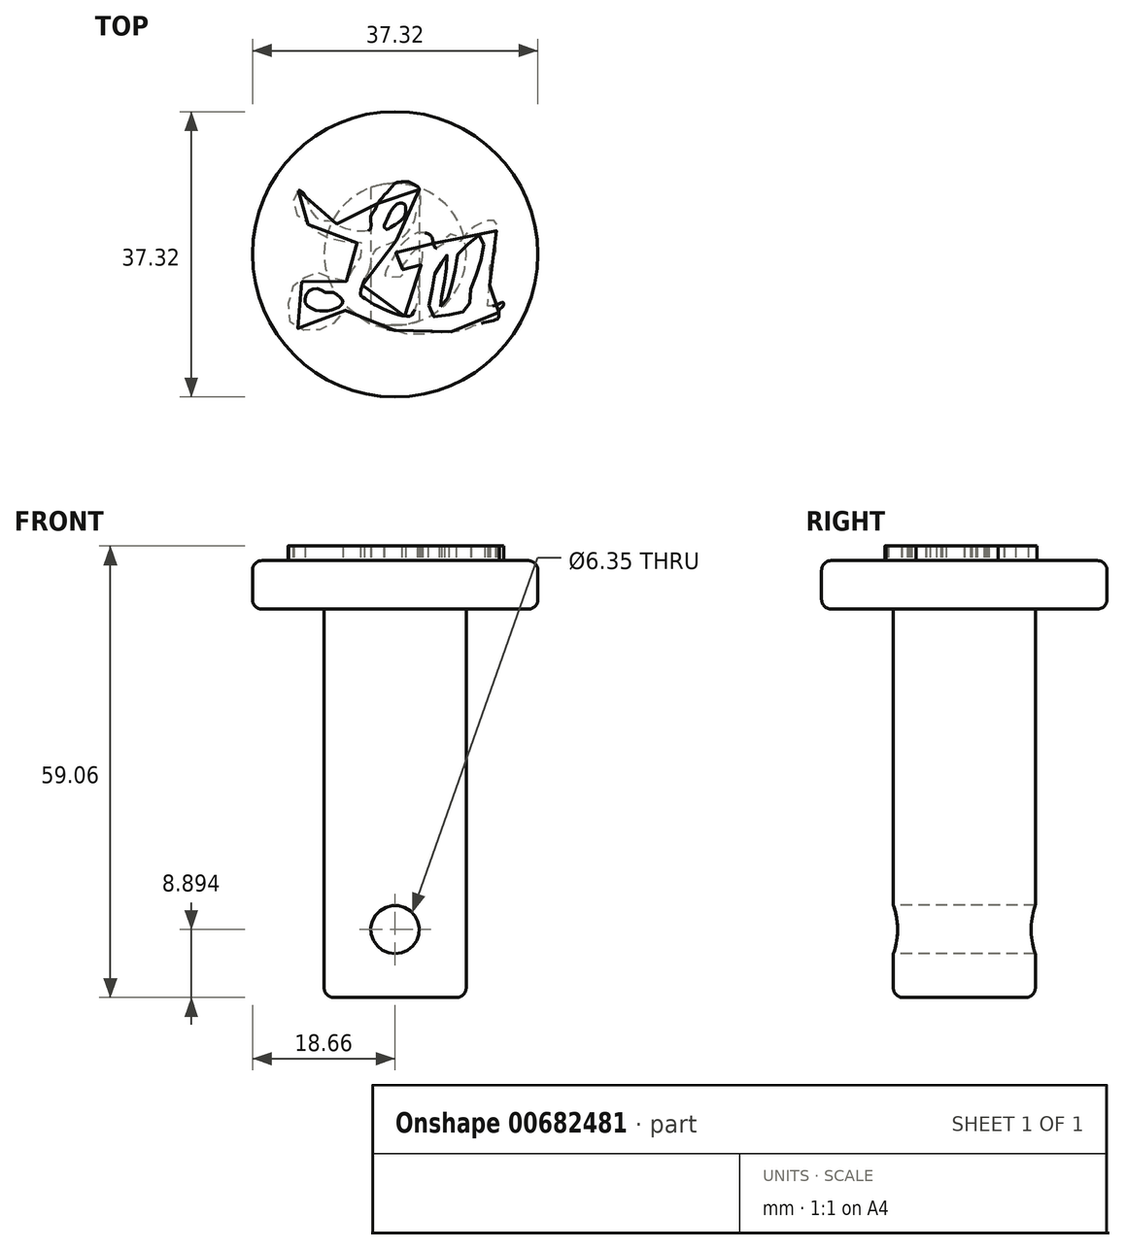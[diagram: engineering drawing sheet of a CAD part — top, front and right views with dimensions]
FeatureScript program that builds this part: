
annotation { "Feature Type Name" : "Feature", "Feature Type Description" : "" }
export const myFeature = defineFeature(function(context is Context, id is Id, definition is map)
    precondition{}
    {
        {
            var Q0;
            Q0=qCreatedBy(makeId("Top.planeOp"),FACE);
            var sketch = newSketch(context, id + "F0", { "sketchPlane" : qUnion([Q0])});
            skCircle(sketch, "E0", {"center": v(0, 0) * mm, "radius": 18.66 * mm});
            skSolve(sketch);
        }
        {
            var Q0;
            Q0=makeQuery(id+"F0.imprint","IMPRINT",FACE,{"disambiguationData":[TD([[makeQuery(id+"F0.imprint","IMPRINT",EDGE,{"derivedFrom":sQuery(id+"F0.wireOp",EDGE,"E0")}),1.0]])]});
            extrude(context, id + "F1", {"entities" : qUnion([Q0]), "depth" : 6.35 * mm, "offsetDistance" : 25.4 * mm});
        }
        {
            var Q0;
            Q0=makeQuery(id+"F1.opExtrude","CAP_FACE",FACE,{"disambiguationData":[OSD([sQuery(id+"F0.wireOp",EDGE,"E0")])],"isStart":true});
            var sketch = newSketch(context, id + "F2", { "sketchPlane" : qUnion([Q0])});
            skCircle(sketch, "E1", {"center": v(0, 0) * mm, "radius": 9.28 * mm});
            skSolve(sketch);
        }
        {
            var Q0;
            Q0=makeQuery(id+"F2.imprint","IMPRINT",FACE,{"disambiguationData":[TD([[makeQuery(id+"F2.imprint","IMPRINT",EDGE,{"derivedFrom":sQuery(id+"F2.wireOp",EDGE,"E1")}),1.0]])]});
            extrude(context, id + "F3", {"entities" : qUnion([Q0]), "operationType" : NewBodyOperationType.ADD, "depth" : 50.8 * mm, "offsetDistance" : 25.4 * mm});
        }
        {
            var Q0;
            Q0=qCreatedBy(makeId("Front.planeOp"),FACE);
            cPlane(context, id + "F4", {"entities" : qUnion([Q0]), "cplaneType" : CPlaneType.OFFSET, "offset" : 19.05 * mm, "width" : 152.4 * mm, "height" : 152.4 * mm});
        }
        {
            var Q0;
            Q0=qCreatedBy(id+"F4.planeOp",FACE);
            var sketch = newSketch(context, id + "F5", { "sketchPlane" : qUnion([Q0])});
            skCircle(sketch, "E2", {"center": v(0, -41.9) * mm, "radius": 3.72 * mm});
            skSolve(sketch);
        }
        {
            var Q0;
            Q0=sQuery(id+"F5.wireOp",VERTEX,"E2.center");
            var Q1;
            Q1=makeQuery(id+"F1.opExtrude","SWEPT_BODY",BODY,{"disambiguationData":[OSD([sQuery(id+"F0.wireOp",EDGE,"E0")])]});
            hole(context, id + "F6", {"style" : HoleStyle.SIMPLE, "endStyle" : HoleEndStyle.THROUGH, "holeDiameter" : 6.35 * mm, "majorDiameter" : 6.35 * mm, "isTappedThrough" : true, "tappedDepth" : 12.7 * mm, "tapClearance" : 3, "locations" : qUnion([Q0]), "scope" : qUnion([Q1])});
        }
        {
            var Q0;
            Q0=makeQuery(id+"F1.opExtrude","CAP_FACE",FACE,{"disambiguationData":[OSD([sQuery(id+"F0.wireOp",EDGE,"E0")])],"isStart":false});
            var sketch = newSketch(context, id + "F7", { "sketchPlane" : qUnion([Q0])});
            skFitSpline(sketch, "E3", {"points": [v(-12.67, 8.37) * mm, v(-13.23, 8.26) * mm, v(-13.23, 7.76) * mm, v(-13.28, 6.99) * mm, v(-13.34, 6.33) * mm, v(-13.11, 5.61) * mm, v(-12.73, 5.17) * mm, v(-12.4, 5.28) * mm, v(-12.12, 4.95) * mm, v(-11.74, 4.4) * mm, v(-11.46, 3.96) * mm, v(-10.96, 3.62) * mm, v(-10.52, 3.13) * mm, v(-9.86, 2.63) * mm, v(-9.36, 2.36) * mm, v(-8.54, 2.08) * mm, v(-7.6, 1.75) * mm, v(-6.6, 1.64) * mm, v(-5.5, 1.47) * mm, v(-4.84, 1.53) * mm, v(-4.34, 1.53) * mm, v(-4.01, 1.2) * mm, v(-4.34, 0) * mm, v(-4.78, -0.79) * mm, v(-5, -1.18) * mm, v(-5.34, -1.62) * mm, v(-5.61, -2.22) * mm, v(-5.89, -2.89) * mm, v(-6.27, -3.44) * mm, v(-6.6, -3.66) * mm, v(-7.38, -3.44) * mm, v(-8.2, -3.16) * mm, v(-9.09, -2.78) * mm, v(-9.75, -2.5) * mm, v(-10.36, -2.39) * mm, v(-11.02, -2.5) * mm, v(-11.74, -2.89) * mm, v(-12.07, -3.5) * mm, v(-12.62, -3.82) * mm, v(-13.28, -4.15) * mm, v(-13.72, -4.76) * mm, v(-14, -5.97) * mm, v(-13.94, -7.24) * mm, v(-13.94, -8.13) * mm, v(-13.72, -8.95) * mm, v(-13.06, -9.56) * mm, v(-12.07, -9.84) * mm, v(-11.07, -9.95) * mm, v(-10.3, -9.9) * mm, v(-9.36, -9.73) * mm, v(-8.65, -9.62) * mm, v(-7.98, -9) * mm, v(-7.27, -8.51) * mm, v(-6.77, -7.74) * mm, v(-6.27, -7.19) * mm, v(-5.78, -7.46) * mm, v(-5.23, -7.85) * mm, v(-4.45, -8.13) * mm, v(-3.8, -8.84) * mm, v(-2.85, -9.23) * mm, v(-2.03, -9.28) * mm, v(-1.42, -9.62) * mm, v(0, -9.95) * mm, v(1.28, -10.33) * mm, v(2.17, -10.39) * mm, v(2.94, -10.39) * mm, v(4.04, -10.39) * mm, v(4.7, -10.28) * mm, v(5.7, -10.17) * mm, v(6.41, -10.22) * mm, v(7.3, -10.11) * mm, v(7.96, -10) * mm, v(9, -9.9) * mm, v(10, -9.45) * mm, v(10.94, -9.12) * mm, v(12.04, -8.84) * mm, v(12.98, -8.62) * mm, v(13.53, -8.3) * mm, v(13.59, -7.8) * mm, v(13.64, -7.24) * mm, v(14.14, -6.75) * mm, v(14.08, -6.3) * mm, v(13.47, -6.53) * mm, v(12.87, -6.75) * mm, v(12.15, -6.91) * mm, v(12.1, -6.75) * mm, v(12.2, -5.86) * mm, v(12.2, -5.1) * mm, v(12.37, -4.1) * mm, v(12.37, -3.38) * mm, v(12.43, -2.44) * mm, v(12.26, -2) * mm, v(12.54, -1.34) * mm, v(12.81, -0.46) * mm, v(13.25, 0.7) * mm, v(13.14, 1.53) * mm, v(13.2, 2.74) * mm, v(13.3, 3.9) * mm, v(13.25, 4.34) * mm, v(12.76, 4.4) * mm, v(12.26, 4.4) * mm, v(11.49, 4.18) * mm, v(10.88, 3.84) * mm, v(10.33, 3.62) * mm, v(9.72, 3.18) * mm, v(9.23, 2.52) * mm, v(8.79, 2.08) * mm, v(8.51, 1.7) * mm, v(8.18, 1.91) * mm, v(8.01, 2.52) * mm, v(7.35, 2.63) * mm, v(6.97, 2.36) * mm, v(6.47, 1.86) * mm, v(6.25, 1.3) * mm, v(5.75, 0.98) * mm, v(5.31, 0.81) * mm, v(4.98, 1.47) * mm, v(4.76, 2.3) * mm, v(4.37, 2.63) * mm, v(3.93, 2.8) * mm, v(3.05, 2.85) * mm, v(2.39, 2.58) * mm, v(1.61, 2.02) * mm, v(0.95, 1.36) * mm, v(0.4, 0.81) * mm, v(0, 0) * mm, v(-0.54, -0.9) * mm, v(-0.92, -1.73) * mm, v(-1.3, -2.22) * mm, v(-1.42, -2.6) * mm, v(-0.81, -3.05) * mm, v(0, -2.89) * mm, v(1, -2.83) * mm, v(1.34, -2.39) * mm, v(0.9, -1.84) * mm, v(1.17, -1.29) * mm, v(1.56, -0.79) * mm, v(1.95, 0) * mm, v(2.28, 0) * mm, v(2.72, 0.7) * mm, v(3.38, 0.98) * mm, v(3.6, 0) * mm, v(3.5, -0.57) * mm, v(3.38, -1.5) * mm, v(3.1, -2.6) * mm, v(2.94, -4.15) * mm, v(3.16, -5.1) * mm, v(2.88, -6.3) * mm, v(2.66, -7.02) * mm, v(2.28, -7.74) * mm, v(1.95, -8.07) * mm, v(0.79, -8.02) * mm, v(-0.54, -7.57) * mm, v(-1.64, -7.13) * mm, v(-2.36, -6.75) * mm, v(-3.24, -6.25) * mm, v(-3.96, -5.75) * mm, v(-4.45, -5.48) * mm, v(-4.5, -4.87) * mm, v(-4.07, -3.5) * mm, v(-3.74, -2.83) * mm, v(-3.35, -2) * mm, v(-3.07, -0.73) * mm, v(-2.58, 0.53) * mm, v(-1.97, 0.98) * mm, v(-1.09, 1.3) * mm, v(0, 1.75) * mm, v(0.84, 2.19) * mm, v(1.67, 2.96) * mm, v(2.17, 3.73) * mm, v(2.5, 4.29) * mm, v(2.83, 5.55) * mm, v(3.27, 6.38) * mm, v(3.32, 7.65) * mm, v(3.1, 8.64) * mm, v(2.44, 9.14) * mm, v(1.72, 9.47) * mm, v(0.84, 9.47) * mm, v(0, 9.3) * mm, v(-0.6, 8.59) * mm, v(-1.25, 7.93) * mm, v(-1.8, 7.26) * mm, v(-2.2, 6.82) * mm, v(-2.63, 5.83) * mm, v(-3.19, 4.95) * mm, v(-3.13, 3.68) * mm, v(-3.4, 3.13) * mm, v(-4.9, 3.02) * mm, v(-6.05, 3.24) * mm, v(-7.32, 3.73) * mm, v(-7.82, 4.12) * mm, v(-9.09, 4.34) * mm, v(-9.97, 4.5) * mm, v(-10.58, 5.17) * mm, v(-10.96, 5.78) * mm, v(-11.35, 6.77) * mm, v(-11.85, 7.76) * mm, v(-12.23, 8.2) * mm, v(-12.67, 8.37) * mm]});
            skFitSpline(sketch, "E4", {"points": [v(-9.12, -4.97) * mm, v(-9.86, -4.58) * mm, v(-10.49, -4.5) * mm, v(-11.23, -4.78) * mm, v(-11.7, -5.4) * mm, v(-11.78, -5.99) * mm, v(-11.66, -6.57) * mm, v(-10.92, -7.08) * mm, v(-10.3, -7.35) * mm, v(-9.67, -7.4) * mm, v(-9.12, -7.43) * mm, v(-8.46, -7.31) * mm, v(-7.87, -7.12) * mm, v(-7.33, -6.92) * mm, v(-6.94, -6.45) * mm, v(-6.86, -5.99) * mm, v(-7.37, -5.52) * mm, v(-7.95, -5.05) * mm, v(-8.58, -5.01) * mm, v(-9.12, -4.97) * mm]});
            skFitSpline(sketch, "E5", {"points": [v(5.92, -6.86) * mm, v(6.3, -6.48) * mm, v(6.72, -6.06) * mm, v(6.92, -5.61) * mm, v(7.17, -4.97) * mm, v(7.3, -4.22) * mm, v(7.58, -3.6) * mm, v(7.69, -2.83) * mm, v(7.93, -1.79) * mm, v(7.97, -1.06) * mm, v(8.2, 0) * mm, v(9, 0.47) * mm, v(9.29, 1.06) * mm, v(10.16, 1.9) * mm, v(10.6, 2.31) * mm, v(11.13, 2.56) * mm, v(11.68, 2.35) * mm, v(11.62, 1.72) * mm, v(11.55, 0.33) * mm, v(11.37, -0.5) * mm, v(10.99, -1.34) * mm, v(10.68, -2.44) * mm, v(10.5, -3) * mm, v(10.23, -3.94) * mm, v(9.91, -4.53) * mm, v(9.91, -5.33) * mm, v(9.84, -6.06) * mm, v(9.67, -6.76) * mm, v(9.6, -7.14) * mm, v(9.08, -7.42) * mm, v(8.49, -7.7) * mm, v(7.97, -7.77) * mm, v(7, -7.94) * mm, v(6.09, -8.15) * mm, v(5.15, -8.18) * mm, v(4.46, -7.94) * mm, v(4.32, -7.42) * mm, v(4.53, -6) * mm, v(4.73, -4.97) * mm, v(4.9, -3.94) * mm, v(5.01, -3.07) * mm, v(5.26, -2.44) * mm, v(5.64, -1.72) * mm, v(6.05, -1.34) * mm, v(6.09, -0.71) * mm, v(6.33, -0.33) * mm, v(6.65, 0) * mm, v(6.96, -0.47) * mm, v(7.03, -1.02) * mm, v(6.72, -1.79) * mm, v(6.47, -2.44) * mm, v(6.47, -3.21) * mm, v(6.4, -4.01) * mm, v(6.2, -4.97) * mm, v(6.05, -5.68) * mm, v(5.88, -6.24) * mm, v(5.74, -6.65) * mm, v(5.92, -6.86) * mm]});
            skFitSpline(sketch, "E6", {"points": [v(-0.13, 6.2) * mm, v(-0.45, 5.84) * mm, v(-0.71, 5.41) * mm, v(-0.97, 4.78) * mm, v(-1.17, 4.32) * mm, v(-1.37, 3.84) * mm, v(-1.46, 3.6) * mm, v(-1.28, 3.38) * mm, v(-1.03, 3.2) * mm, v(-0.82, 3.37) * mm, v(-0.57, 3.52) * mm, v(-0.28, 3.67) * mm, v(0, 3.9) * mm, v(0.49, 4.18) * mm, v(0.9, 4.56) * mm, v(1.2, 4.98) * mm, v(1.34, 5.41) * mm, v(1.4, 5.98) * mm, v(1.29, 6.52) * mm, v(1, 6.65) * mm, v(0.68, 6.7) * mm, v(0.3, 6.6) * mm, v(-0.13, 6.2) * mm]});
            skSolve(sketch);
        }
        {
            var Q0;
            Q0=makeQuery(id+"F7.imprint","IMPRINT",FACE,{"disambiguationData":[TD([[makeQuery(id+"F7.imprint","IMPRINT",EDGE,{"derivedFrom":sQuery(id+"F7.wireOp",EDGE,"E3")}),1.0]])]});
            extrude(context, id + "F8", {"entities" : qUnion([Q0]), "operationType" : NewBodyOperationType.ADD, "depth" : 1.9 * mm, "offsetDistance" : 25.4 * mm});
        }
        {
            var Q0;
            Q0=makeQuery(id+"F1.opExtrude","CAP_EDGE",EDGE,{"disambiguationData":[OSD([sQuery(id+"F0.wireOp",EDGE,"E0")])],"isStart":false});
            var Q1;
            Q1=makeQuery(id+"F1.opExtrude","CAP_EDGE",EDGE,{"disambiguationData":[OSD([sQuery(id+"F0.wireOp",EDGE,"E0")])],"isStart":true});
            var Q2;
            Q2=makeQuery(id+"F3.opExtrude","CAP_EDGE",EDGE,{"disambiguationData":[OSD([sQuery(id+"F2.wireOp",EDGE,"E1")])],"isStart":false});
            var Q3;
            Q3=makeQuery(id+"F6.hole-0.boolean.opBoolean","INTERSECT",EDGE,{"disambiguationData":[OD(0.0)],"derivedFrom":[makeQuery(id+"F3.opExtrude","SWEPT_FACE",FACE,{"disambiguationData":[OSD([sQuery(id+"F2.wireOp",EDGE,"E1")])]}),makeQuery(id+"F6.hole-0.opRevolve","SWEPT_FACE",FACE,{"disambiguationData":[OSD([sQuery(id+"F6.hole-0.sketch.wireOp",EDGE,"core_line_2")])]})]});
            var Q4;
            Q4=makeQuery(id+"F6.hole-0.boolean.opBoolean","INTERSECT",EDGE,{"disambiguationData":[OD(1.0)],"derivedFrom":[makeQuery(id+"F3.opExtrude","SWEPT_FACE",FACE,{"disambiguationData":[OSD([sQuery(id+"F2.wireOp",EDGE,"E1")])]}),makeQuery(id+"F6.hole-0.opRevolve","SWEPT_FACE",FACE,{"disambiguationData":[OSD([sQuery(id+"F6.hole-0.sketch.wireOp",EDGE,"core_line_2")])]})]});
            fillet(context, id + "F9", {"entities" : qUnion([Q0, Q1, Q2, Q3, Q4]), "radius" : 1.27 * mm, "tangentPropagation" : true, "allowEdgeOverflow" : false});
        }
    });
